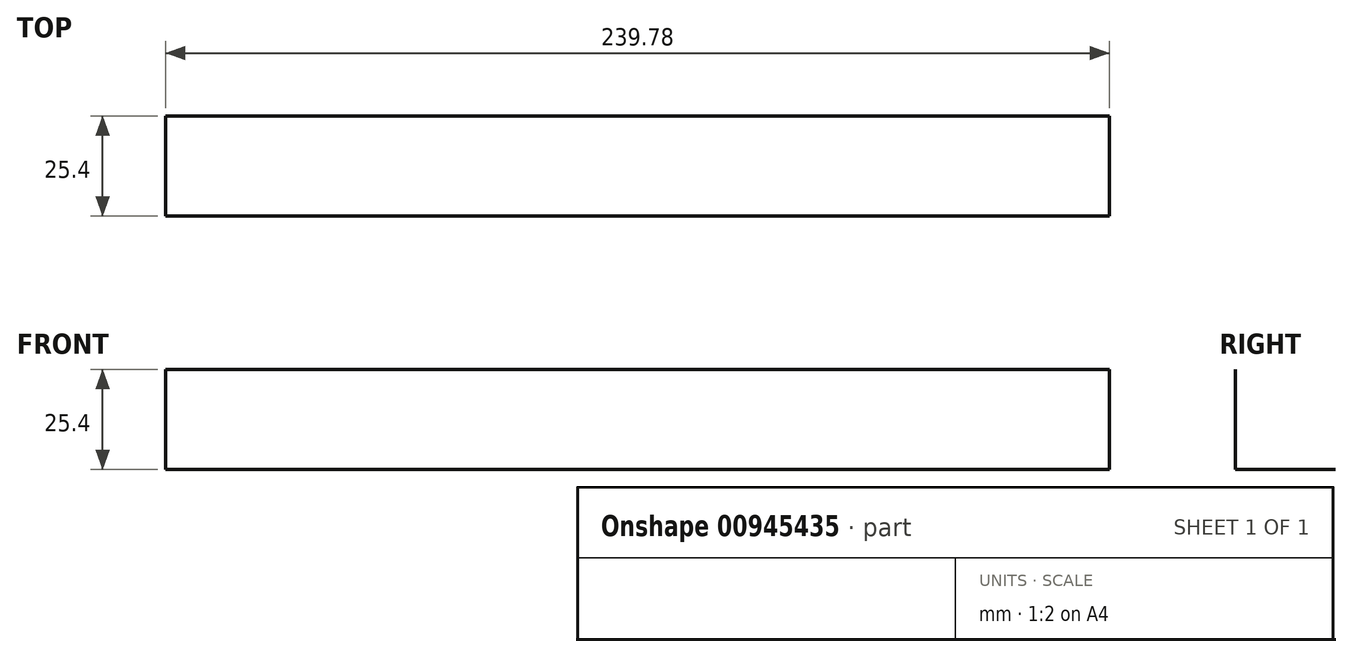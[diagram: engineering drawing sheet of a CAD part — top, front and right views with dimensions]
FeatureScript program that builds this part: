
annotation { "Feature Type Name" : "Feature", "Feature Type Description" : "" }
export const myFeature = defineFeature(function(context is Context, id is Id, definition is map)
    precondition{}
    {
        {
            var Q0;
            Q0=qCreatedBy(makeId("Right.planeOp"),FACE);
            var sketch = newSketch(context, id + "F0", { "sketchPlane" : qUnion([Q0])});
            skLineSegment(sketch, "E0.top", {"start": v(-7.57, -17.22) * mm, "end": v(-32.97, -17.22) * mm});
            skLineSegment(sketch, "E0.right", {"start": v(-32.97, 8.18) * mm, "end": v(-32.97, -17.22) * mm});
            skSolve(sketch);
        }
        {
            var Q0;
            Q0=sQuery(id+"F0.wireOp",EDGE,"E0.right");
            var Q1;
            Q1=sQuery(id+"F0.wireOp",EDGE,"E0.top");
            extrude(context, id + "F1", {"bodyType" : ToolBodyType.SURFACE, "surfaceEntities" : qUnion([Q0, Q1]), "depth" : 239.78 * mm, "offsetDistance" : 25.4 * mm});
        }
    });
